# Revit family: Reduzierwinkel Endabschlussblech DD, FS, FT SO
name_source: partatom
category: Generic Models
revit_build: Autodesk Revit 2017 (Build: 20160225_1515(x64)
units: mm (PartAtom-declared; Revit-internal decimal feet)

## family parameters
Always vertical = Yes
Can host rebar = No
Cut with Voids When Loaded = No
Part Type = Normal
Room Calculation Point = No
Round Connector Dimension = Use Diameter
Shared = No
Work Plane-Based = No

## types (3) — shared parameters
Height = 110 mm  [stored 0.360892 ft]
Height 1 = 17 mm
Height 2 = 14 mm  [stored 0.0459318 ft]
Manufacturer = OBO Bettermann
URL = http://www.obo-bettermann.com
Width = 300 mm
Width 1 = 395 mm  [stored 1.29593 ft]

## per-type parameters (varying)
| type | GTIN | Manufacturer Art.No. | Material |
| RWEB 130 DD | 4012196241156 | 7107501 | Strip galvanised zinc/aluminium, Double Dip |
| RWEB 130 FS | 4012196243013 | 7111304 | Strip-galvanised |
| RWEB 130 FT SO | 4012195624066 | 7195355 | Hot-dip galvanised 85 µm |

note: column(s) folded — value = type name in every type: Article Type

note: [stored X ft] marks values corroborated as IEEE doubles in the binary element streams (Revit-internal decimal feet)
